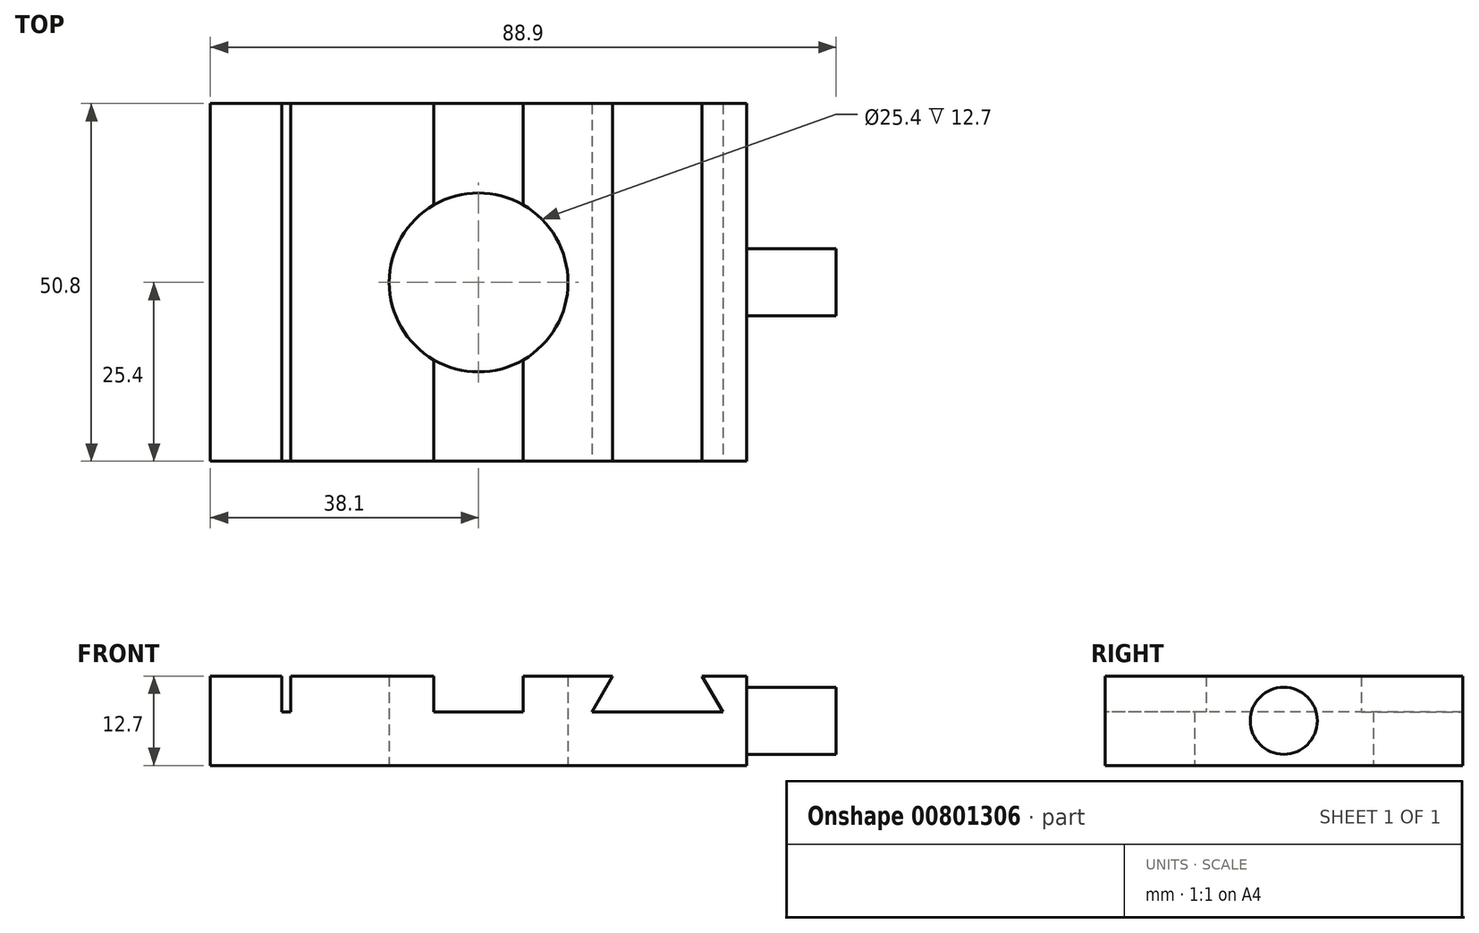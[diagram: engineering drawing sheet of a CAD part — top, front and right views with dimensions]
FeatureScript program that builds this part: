
annotation { "Feature Type Name" : "Feature", "Feature Type Description" : "" }
export const myFeature = defineFeature(function(context is Context, id is Id, definition is map)
    precondition{}
    {
        {
            var Q0;
            Q0=qCreatedBy(makeId("Top.planeOp"),FACE);
            var sketch = newSketch(context, id + "F0", { "sketchPlane" : qUnion([Q0])});
            skLineSegment(sketch, "E0.bottom", {"start": v(38.1, -25.4) * mm, "end": v(-38.1, -25.4) * mm});
            skLineSegment(sketch, "E0.top", {"start": v(38.1, 25.4) * mm, "end": v(-38.1, 25.4) * mm});
            skLineSegment(sketch, "E0.left", {"start": v(38.1, -25.4) * mm, "end": v(38.1, 25.4) * mm});
            skLineSegment(sketch, "E0.right", {"start": v(-38.1, -25.4) * mm, "end": v(-38.1, 25.4) * mm});
            skPoint(sketch, "E0.middle", {"position": v(0, 0) * mm});
            skCircle(sketch, "E1", {"center": v(0, 0) * mm, "radius": 12.7 * mm});
            skSolve(sketch);
        }
        {
            var Q0;
            Q0=makeQuery(id+"F0.imprint","IMPRINT",FACE,{"disambiguationData":[TD([[makeQuery(id+"F0.imprint","IMPRINT",EDGE,{"derivedFrom":sQuery(id+"F0.wireOp",EDGE,"E0.bottom")}),-1.0]])]});
            extrude(context, id + "F1", {"entities" : qUnion([Q0]), "depth" : 12.7 * mm, "offsetDistance" : 25.4 * mm});
        }
        {
            var Q0;
            Q0=makeQuery(id+"F1.opExtrude","CAP_FACE",FACE,{"disambiguationData":[OSD([sQuery(id+"F0.wireOp",EDGE,"E0.bottom"),sQuery(id+"F0.wireOp",EDGE,"E0.top"),sQuery(id+"F0.wireOp",EDGE,"E0.left"),sQuery(id+"F0.wireOp",EDGE,"E0.right"),sQuery(id+"F0.wireOp",EDGE,"E1")])],"isStart":false});
            var sketch = newSketch(context, id + "F2", { "sketchPlane" : qUnion([Q0])});
            skLineSegment(sketch, "E2.bottom", {"start": v(-27.94, 25.4) * mm, "end": v(-26.67, 25.4) * mm});
            skLineSegment(sketch, "E2.top", {"start": v(-27.94, -25.4) * mm, "end": v(-26.67, -25.4) * mm});
            skLineSegment(sketch, "E2.left", {"start": v(-27.94, 25.4) * mm, "end": v(-27.94, -25.4) * mm});
            skLineSegment(sketch, "E2.right", {"start": v(-26.67, 25.4) * mm, "end": v(-26.67, -25.4) * mm});
            skLineSegment(sketch, "E3", {"start": v(-6.35, 25.4) * mm, "end": v(-6.35, -25.4) * mm});
            skLineSegment(sketch, "E4", {"start": v(-6.35, -25.4) * mm, "end": v(6.35, -25.4) * mm});
            skLineSegment(sketch, "E5", {"start": v(6.35, -25.4) * mm, "end": v(6.35, 25.4) * mm});
            skLineSegment(sketch, "E6", {"start": v(6.35, 25.4) * mm, "end": v(-6.35, 25.4) * mm});
            skPoint(sketch, "E7", {"position": v(0, 0) * mm});
            skLineSegment(sketch, "E8", {"start": v(0, 25.4) * mm, "end": v(0, -25.4) * mm, "construction": true});
            skSolve(sketch);
        }
        {
            var Q0;
            Q0=makeQuery(id+"F2.imprint","IMPRINT",FACE,{"disambiguationData":[TD([[makeQuery(id+"F2.imprint","IMPRINT",EDGE,{"derivedFrom":sQuery(id+"F2.wireOp",EDGE,"E2.bottom")}),1.0]])]});
            var Q1;
            {var subQ0=sQuery(id+"F2.wireOp",EDGE,"E6");Q1=makeQuery(id+"F2.imprint","IMPRINT",FACE,{"disambiguationData":[TD([[makeQuery(id+"F2.imprint","IMPRINT",EDGE,{"derivedFrom":subQ0}),1.0]])]});}
            var Q2;
            {var subQ0=sQuery(id+"F2.wireOp",EDGE,"E3");var subQ1=makeQuery(id+"F1.opExtrude","CAP_EDGE",EDGE,{"disambiguationData":[OSD([sQuery(id+"F0.wireOp",EDGE,"E1")])],"isStart":false});var subQ2=makeQuery(id+"F2.imprint","INTERSECT",VERTEX,{"disambiguationData":[OD(0.0)],"derivedFrom":[subQ1,subQ0]});Q2=makeQuery(id+"F2.imprint","IMPRINT",FACE,{"disambiguationData":[TD([[makeQuery(id+"F2.imprint","IMPRINT",EDGE,{"disambiguationData":[TD([[subQ2,-1.0]])],"derivedFrom":subQ0}),1.0]])]});}
            var Q3;
            {var subQ0=sQuery(id+"F2.wireOp",EDGE,"E4");Q3=makeQuery(id+"F2.imprint","IMPRINT",FACE,{"disambiguationData":[TD([[makeQuery(id+"F2.imprint","IMPRINT",EDGE,{"derivedFrom":subQ0}),-1.0]])]});}
            extrude(context, id + "F3", {"entities" : qUnion([Q0, Q1, Q2, Q3]), "operationType" : NewBodyOperationType.REMOVE, "oppositeDirection" : true, "depth" : 5.08 * mm, "offsetDistance" : 25.4 * mm});
        }
        {
            var Q0;
            Q0=makeQuery(id+"F1.opExtrude","SWEPT_FACE",FACE,{"disambiguationData":[OSD([sQuery(id+"F0.wireOp",EDGE,"E0.bottom")])]});
            var sketch = newSketch(context, id + "F4", { "sketchPlane" : qUnion([Q0])});
            skLineSegment(sketch, "E9", {"start": v(19.05, 12.7) * mm, "end": v(16.12, 7.62) * mm});
            skLineSegment(sketch, "E10", {"start": v(16.12, 7.62) * mm, "end": v(34.68, 7.62) * mm});
            skLineSegment(sketch, "E11", {"start": v(34.68, 7.62) * mm, "end": v(31.75, 12.7) * mm});
            skLineSegment(sketch, "E12", {"start": v(31.75, 12.7) * mm, "end": v(19.05, 12.7) * mm});
            skLineSegment(sketch, "E13", {"start": v(25.4, 7.62) * mm, "end": v(25.4, 12.7) * mm, "construction": true});
            skSolve(sketch);
        }
        {
            var Q0;
            Q0=makeQuery(id+"F4.imprint","IMPRINT",FACE,{"disambiguationData":[TD([[makeQuery(id+"F4.imprint","IMPRINT",EDGE,{"derivedFrom":sQuery(id+"F4.wireOp",EDGE,"E9")}),1.0]])]});
            extrude(context, id + "F5", {"entities" : qUnion([Q0]), "operationType" : NewBodyOperationType.REMOVE, "endBound" : BoundingType.THROUGH_ALL, "oppositeDirection" : true, "depth" : 25.4 * mm, "offsetDistance" : 25.4 * mm});
        }
        {
            var Q0;
            Q0=makeQuery(id+"F1.opExtrude","SWEPT_FACE",FACE,{"disambiguationData":[OSD([sQuery(id+"F0.wireOp",EDGE,"E0.left")])]});
            var sketch = newSketch(context, id + "F6", { "sketchPlane" : qUnion([Q0])});
            skCircle(sketch, "E14", {"center": v(0, 6.35) * mm, "radius": 4.76 * mm});
            skPoint(sketch, "E14.centerSnap0", {"position": v(-25.4, 6.35) * mm});
            skPoint(sketch, "E14.centerSnap1", {"position": v(0, 12.7) * mm});
            skSolve(sketch);
        }
        {
            var Q0;
            Q0=makeQuery(id+"F6.imprint","IMPRINT",FACE,{"disambiguationData":[TD([[makeQuery(id+"F6.imprint","IMPRINT",EDGE,{"derivedFrom":sQuery(id+"F6.wireOp",EDGE,"E14")}),1.0]])]});
            extrude(context, id + "F7", {"entities" : qUnion([Q0]), "operationType" : NewBodyOperationType.ADD, "depth" : 12.7 * mm, "offsetDistance" : 25.4 * mm});
        }
    });
